# Revit family: AHUKZ-01B_LC23013
name_source: partatom
category: Aparatos eléctricos
revit_build: Autodesk Revit 2016 (Build: 20150220_1215(x64)
units: mm (PartAtom-declared; Revit-internal decimal feet)

## family parameters
Compartido = No
Corte con vacíos al cargar = No
Cota de conector redondo = Diámetro de uso
Mantener orientación de anotación = No
Número OmniClass = 23.80.00.00
Punto de cálculo de habitación = No
Se basa en plano de trabajo = No
Siempre vertical = Sí
Tipo de pieza = Caja de conexiones
Título OmniClass = Electric Power and Lighting

## types (1)
- AHUKZ-B
    Alimentación = 220-240 ~50Hz / 208-230 ~60 Hz
    Capacidad = 14kW (9 ~ 20)
    Costo = 0 $
    Código de montaje = LC23013
    Descripción = CAJAS DE CONTROL COMBINABLE PARA UTA
    Dimensiones = 375 x 350 x 150 mm
    Entrada líquido = 7,9 mm (5/16")
    Fabricante = SALVADOR ESCODA
    Imagen de tipo = ahukz-b.png
    Modelo = AHUKZ-01B
    Salida líquido = 7,9 mm (5/16")
    URL = www.salvadorescoda.com
